# Revit family: QF_ELECTROLUXPROFESSIONAL_1LSNSS_TD6-30_E
name_source: partatom
category: Attrezzature speciali
units: mm (PartAtom-declared; Revit-internal decimal feet)

## family parameters
Basato su piano di lavoro = No
Condiviso = No
Punto di calcolo locali = No
Quota connettore circolare = Usa diametro
Sempre verticale = Sì
Taglio con vuoti quando caricato = No
Tipo di parte = Normale

## types (51) — shared parameters
Depth Actual = 1365 mm  [stored 4.47835 ft]
Height Actual = 1855 mm  [stored 6.08596 ft]
Latent Heat Output = 0.0
Length Actual = 960 mm  [stored 3.14961 ft]
Modello = TD6-30
Phase = 3
Produttore = Electrolux Professional
Sensible Heat Output = 0.0
URL = www.electroluxprofessional.com
Weight = 280
zero-valued in all types: Gas KW, Prospetto di default

## per-type parameters (varying)
| type | Cycle | Descrizione | Item Number | Steam Pounds per Hour | Volts | Watts |
| 9872330020 | 50 Hz | TUMBLE DRYER TD6-30 30KG/67LB SST DRUM EL 32KW 230/50/3 COMPASS PRO 6G81 SLVR/SLVR DO.RIGHT REV MB STOP DISCON DMPR | 1L0G58 | 0 | 230 V | 33500 W |
| 9872330070 | 50 Hz | TUMBLE DRYER TD6-30 30KG/67LB SST DRUM EL 32KW 380-415/50/3N COMPASS PRO 6G81 SST/SLVR DO.LEFT REV MB STOP DISCON DMPR | 1LSP9R | 0 | 415 V | 33500 W |
| 9872330008 | 50 Hz | TUMBLE DRYER TD6-30 30KG/67LB SST DRUM EL 32KW 400/50/3N COMPASS PRO 6G81 SLVR/SLVR DO.RIGHT REV MB STOP DISCON DMPR | 1L0G3E | 0 | 400 V | 33500 W |
| 9872330085 | 50 Hz | TUMBLE DRYER TD6-30 30KG/67LB GALVA.DRUM EL 32KW 380-415/50/3 COMPASS PRO 6G82 SLVR/SLVR DO.RIGHT REV STOP DISCON DMPR | 1L0GS4 | 0 | 415 V | 33500 W |
| 9872330028 | 50 Hz | TUMBLE DRYER TD6-30 30KG/67LB SST DRUM EL 32KW 400/50/3N COMPASS PRO 6G82 SST/SST DO.RIGHT REV DISCON DMPR | 1L0G5G | 0 | 400 V | 33500 W |
| 9872330048 | 50 Hz | TUMBLE DRYER TD6-30 30KG/67LB SST DRUM EL 32KW 400/50/3N COMPASS PRO 6G81 SLVR/SLVR DO.LEFT REV MB STOP DISCON DMPR | 1L0G5V | 0 | 400 V | 33500 W |
| 9872330058 | 50 Hz | TUMBLE DRYER TD6-30 30KG/67LB SST DRUM EL 32KW 400/50/3N COMPASS PRO 6G81 SLVR/SLVR DO.RIGHT REV MB STOP DISCON DMPR | 1L0GAU | 0 | 400 V | 33500 W |
| 9872330141 | 50 Hz | TUMBLE DRYER TD6-30 30KG/67LB SST DRUM EL 32KW 200/50/3 COMPASS PRO 6G86 SLVR/SLVR DO.RIGHT REV DISCON DMPR | 1L0H7W | 0 | 200 V | 33500 W |
| 9872330151 | 50 Hz | TUMBLE DRYER TD6-30 30KG/67LB SST DRUM EL 24KW 400/50/3 COMPASS PRO 6G82 SLVR/SLVR DO.LEFT REV STOP DISCON DMPR | 1L0HDF | 0 | 400 V | 25500 W |
| 9872330005 | 60 Hz | TUMBLE DRYER TD6-30 MARINE 30KG/67LB GALVA.DRUM EL 32KW 440/60/3 COMPASS PRO 6G82 SST/SLVR DO.RIGHT REV DISCON DMPR | 1L0G50 | 0 | 440 V | 33500 W |
| 9872330139 | 50 Hz | TUMBLE DRYER TD6-30 30KG/67LB GALVA.DRUM EL 24KW 230/50/3 COMPASS PRO 6G81 SLVR/SLVR DO.RIGHT REV MB STOP DISCON DMPR | 1L0H56 | 0 | 230 V | 25500 W |
| 9872330092 | 60 Hz | TUMBLE DRYER TD6-30 30KG/67LB GALVA.DRUM EL 24KW 400/60/3 COMPASS PRO 6G82 SLVR/SLVR DO.RIGHT REV DISCON DMPR | 1LA23L | 0 | 400 V | 25500 W |
| 9872330055 | 50 Hz | TUMBLE DRYER TD6-30 MARINE 30KG/67LB SST DRUM EL 24KW 380-415/50/3 COMPASS PRO 6G82 SLVR/SLVR DO.RIGHT REV STOP DISC... | 1LSP7L | 0 | 415 V | 25200 W |
| 9872330075 | 60 Hz | TUMBLE DRYER TD6-30 30KG/67LB SST DRUM EL 32KW 440/60/3 COMPASS PRO 6G81 SLVR/SLVR DO.RIGHT REV MB STOP DISCON DMPR | 1L0GF8 | 0 | 440 V | 33500 W |
| 9872330012 | 50 Hz | TUMBLE DRYER TD6-30 30KG/67LB GALVA.DRUM EL 32KW 400/50/3N COMPASS PRO 6G82 SLVR/SLVR DO.RIGHT REV STOP DISCON DMPR | 1L0G3J | 0 | 400 V | 33500 W |
| 9872330022 | 60 Hz | TUMBLE DRYER TD6-30 MARINE 30KG/67LB GALVA.DRUM EL 32KW 440/60/3 COMPASS PRO 6G82 SLVR/SLVR DO.LEFT REV DISCON DMPR | 1L0G5A | 0 | 440 V | 33500 W |
| 9872330144 | 60 Hz | TUMBLE DRYER TD6-30 30KG/67LB SST DRUM EL 24KW 200/60/3 COMPASS PRO 6L85 SLVR/SLVR DO.RIGHT REV DISCON DMPR | 1L0H94 | 0 | 200 V | 25500 W |
| 9872330027 | 50 Hz | TUMBLE DRYER TD6-30 30KG/67LB SST DRUM EL 32KW 400/50/3N COMPASS PRO 6G81 SST/SLVR DO.RIGHT REV MB DISCON DMPR | 1L0G5F | 0 | 400 V | 33500 W |
| 9872330057 | 50 Hz | TUMBLE DRYER TD6-30 30KG/67LB GALVA.DRUM EL 24KW 400/50/3N COMPASS PRO 6G81 SLVR/SLVR DO.RIGHT REV MB STOP DISCON DMPR | 1L8247 | 0 | 400 V | 25500 W |
| 9872330077 | 60 Hz | TUMBLE DRYER TD6-30 30KG/67LB GALVA.DRUM EL 24KW 230/60/3 COMPASS PRO 6G82 SLVR/SLVR DO.RIGHT REV DISCON DMPR | 1L0GJD | 0 | 230 V | 25500 W |
| 9872330094 | 60 Hz | TUMBLE DRYER TD6-30 MARINE 30KG/67LB GALVA.DRUM EL 32KW 480/60/3 COMPASS PRO 6G82 SLVR/SLVR DO.RIGHT REV DISCON DMPR | 1LSPEW | 0 | 480 V | 33500 W |
| 9872330136 | 60 Hz | TUMBLE DRYER TD6-30 30KG/67LB SST DRUM EL 32KW 200/60/3 COMPASS PRO 6G86 SLVR/SLVR DO.RIGHT REV DISCON DMPR | 1LT5ZB | 0 | 200 V | 33500 W |
| 9872330156 | 50 Hz | TUMBLE DRYER TD6-30 MARINE 30KG/67LB GALVA.DRUM EL 24KW 400/50/3 COMPASS PRO 6G82 SLVR/SLVR DO.RIGHT REV STOP DISCON... | 1LT65D | 0 | 400 V | 25500 W |
| 9872330166 | 50 Hz | TUMBLE DRYER TD6-30 30KG/67LB SST DRUM EL 32KW 380-415/50/3N COMPASS PRO 6G81 SST/SST DO.LEFT REV MB STOP DISCON DMPR | 1LT6J9 | 65 | 415 V | 33500 W |
| 9872330004 | 50 Hz | TUMBLE DRYER TD6-30 30KG/67LB GALVA.DRUM EL 24KW 415/50/3 COMPASS PRO 6G81 SLVR/SLVR DO.RIGHT REV MB STOP DISCON DMPR | 1L0G4Z | 0 | 415 V | 25500 W |
| 9872330081 | 60 Hz | TUMBLE DRYER TD6-30 30KG/67LB SST DRUM EL 32KW 400/60/3N COMPASS PRO 6G81 SST/SLVR DO.RIGHT REV MB STOP DISCON DMPR | 1L0GKP | 0 | 400 V | 33500 W |
| 9872330024 | 50 Hz | TUMBLE DRYER TD6-30 30KG/67LB GALVA.DRUM EL 24KW 400/50/3 COMPASS PRO 6G82 SLVR/SLVR DO.RIGHT REV STOP DISCON DMPR | 1L0G5C | 0 | 400 V | 25500 W |
| 9872330021 | 50 Hz | TUMBLE DRYER TD6-30 30KG/67LB SST DRUM EL 32KW 400/50/3 COMPASS PRO 6G82 SST/SLVR DO.RIGHT REV DISCON DMPR | 1L0G59 | 0 | 400 V | 33500 W |
| 9872330089 | 60 Hz | TUMBLE DRYER TD6-30 MARINE 30KG/67LB GALVA.DRUM EL 32KW 400/60/3 COMPASS PRO 6G81 SLVR/SLVR DO.RIGHT REV MB DISCON DMPR | 1L0GUD | 0 | 400 V | 33500 W |
| 9872330099 | 60 Hz | TUMBLE DRYER TD6-30 MARINE 30KG/67LB GALVA.DRUM EL 32KW 230/60/3 COMPASS PRO 6G82 SST/SLVR DO.RIGHT REV DISCON DMPR | 1L0GW8 | 0 | 230 V | 33500 W |
| 9872330145 | 50 Hz | TUMBLE DRYER TD6-30 30KG/67LB SST DRUM EL 24KW 200/50/3 COMPASS PRO 6L85 SLVR/SLVR DO.RIGHT REV DISCON DMPR | 1L0H95 | 0 | 200 V | 25500 W |
| 9872330071 | 60 Hz | TUMBLE DRYER TD6-30 30KG/67LB GALVA.DRUM EL 32KW 230/60/3 COMPASS PRO 6G81 SLVR/SLVR DO.RIGHT REV MB DISCON DMPR | 1LSP9S | 0 | 230 V | 33500 W |
| 9872330125 | 60 Hz | TUMBLE DRYER TD6-30 30KG/67LB SST DRUM EL 32KW 230/60/3 COMPASS PRO 6G82 SST/SST DO.LEFT REV STOP DISCON DMPR | 1LSPSW | 0 | 230 V | 33500 W |
| 9872330165 | 50 Hz | TUMBLE DRYER TD6-30 30KG/67LB SST DRUM EL 32KW 400/50/3N COMPASS PRO 6L85 2.I/O SLVR/SLVR DO.LEFT EXT.PM. REV DISCON... | 1LT6GK | 65 | 400 V | 33500 W |
| 9872330009 | 50 Hz | TUMBLE DRYER TD6-30 30KG/67LB GALVA.DRUM EL 32KW 400/50/3N COMPASS PRO 6G82 SLVR/SLVR DO.RIGHT REV DISCON DMPR | 1L0G3F | 0 | 400 V | 33500 W |
| 9872330019 | 60 Hz | TUMBLE DRYER TD6-30 30KG/67LB SST DRUM EL 32KW 400/60/3N COMPASS PRO 6G82 SLVR/SLVR DO.RIGHT REV DISCON DMPR | 1L0G57 | 0 | 400 V | 33500 W |
| 9872330110 | 60 Hz | TUMBLE DRYER TD6-30 30KG/67LB SST DRUM EL 32KW 480/60/3 COMPASS PRO 6G82 SST/SLVR DO.RIGHT REV DISCON DMPR | 1L0GYR | 0 | 480 V | 33500 W |
| 9872330120 | 50 Hz | TUMBLE DRYER TD6-30 30KG/67LB SST DRUM EL 32KW 415/50/3N COMPASS PRO 6G82 SST/SST DO.RIGHT REV STOP DISCON DMPR | 1LSPPJ | 0 | 415 V | 33500 W |
| 9872330049 | 50 Hz | TUMBLE DRYER TD6-30 30KG/67LB GALVA.DRUM EL 18KW 400/50/3N COMPASS PRO 6G81 SLVR/SLVR DO.RIGHT REV MB DISCON DMPR | 1L0G5W | 0 | 400 V | 19500 W |
| 9872330140 | 50 Hz | TUMBLE DRYER TD6-30 MARINE 30KG/67LB SST DRUM EL 24KW 380-415/50/3 COMPASS PRO 6G82 SST/SST DO.RIGHT REV STOP DISCON... | 1L0H70 | 0 | 415 V | 25200 W |
| 9872330150 | 50 Hz | TUMBLE DRYER TD6-30 30KG/67LB SST DRUM EL 32KW 400/50/3 COMPASS PRO 6G82 SST/SLVR DO.RIGHT REV STOP DISCON DMPR | 1L0HAN | 0 | 400 V | 33500 W |
| 9872330108 | 50 Hz | TUMBLE DRYER TD6-30 30KG/67LB SST DRUM EL 24KW 400/50/3N COMPASS PRO 6G81 SLVR/SLVR DO.RIGHT REV MB STOP DISCON DMPR | 1LSPL1 | 0 | 400 V | 25500 W |
| 9872330006 | 50 Hz | TUMBLE DRYER TD6-30 30KG/67LB GALVA.DRUM EL 24KW 415/50/3N COMPASS PRO 6G81 SLVR/SLVR DO.RIGHT REV MB STOP DISCON DMPR | 1L0G51 | 0 | 415 V | 25500 W |
| 9872330016 | 50 Hz | TUMBLE DRYER TD6-30 30KG/67LB SST DRUM EL 32KW 400/50/3N COMPASS PRO 6G82 SLVR/SLVR DO.RIGHT REV STOP DISCON DMPR | 1L0G54 | 0 | 400 V | 33500 W |
| 9872330083 | 50 Hz | TUMBLE DRYER TD6-30 MARINE 30KG/67LB GALVA.DRUM EL 32KW 400/50/3 COMPASS PRO 6G82 SST/SLVR DO.RIGHT REV DISCON DMPR | 1L0GS0 | 0 | 400 V | 33500 W |
| 9872330023 | 60 Hz | TUMBLE DRYER TD6-30 30KG/67LB GALVA.DRUM EL 32KW 480/60/3 COMPASS PRO 6G82 SST/SLVR DO.RIGHT REV DISCON DMPR | 1L0G5B | 0 | 480 V | 33500 W |
| 9872330137 | 60 Hz | TUMBLE DRYER TD6-30 MARINE 30KG/67LB SST DRUM EL 24KW 480/60/3 COMPASS PRO 6G82 SLVR/SLVR DO.LEFT REV STOP DISCON DMPR | 1LT60L | 0 | 480 V | 25500 W |
| 9872330063 | 50 Hz | TUMBLE DRYER TD6-30 30KG/67LB GALVA.DRUM EL 32KW 380-415/50/3N COMPASS PRO 6L80 SLVR/SLVR DO.RIGHT REV DISCON DMPR | 1L0GCK | 0 | 415 V | 33500 W |
| 9872330157 | 60 Hz | TUMBLE DRYER TD6-30 30KG/67LB SST DRUM EL 32KW 440/60/3 COMPASS PRO 6G81 SST/SLVR DO.RIGHT REV MB STOP DISCON DMPR | 1LT65L | 0 | 440 V | 33500 W |
| 9872330162 | 60 Hz | TUMBLE DRYER TD6-30 MARINE 30KG/67LB SST DRUM EL 32KW 480/60/3 COMPASS PRO 6G82 SLVR/SLVR DO.RIGHT REV STOP DISCON DMPR | 1LT69V | 0 | 480 V | 33500 W |
| 9872330010 | 50 Hz | TUMBLE DRYER TD6-30 30KG/67LB GALVA.DRUM EL 32KW 400/50/3N COMPASS PRO 6G81 SLVR/SLVR DO.RIGHT REV MB STOP DISCON DMPR | 1L0G3G | 0 | 400 V | 33500 W |

note: [stored X ft] marks values corroborated as IEEE doubles in the binary element streams (Revit-internal decimal feet)

## geometry (parser evidence)
native form markers: Blend x8
no freeform markers — native parametric forms only
